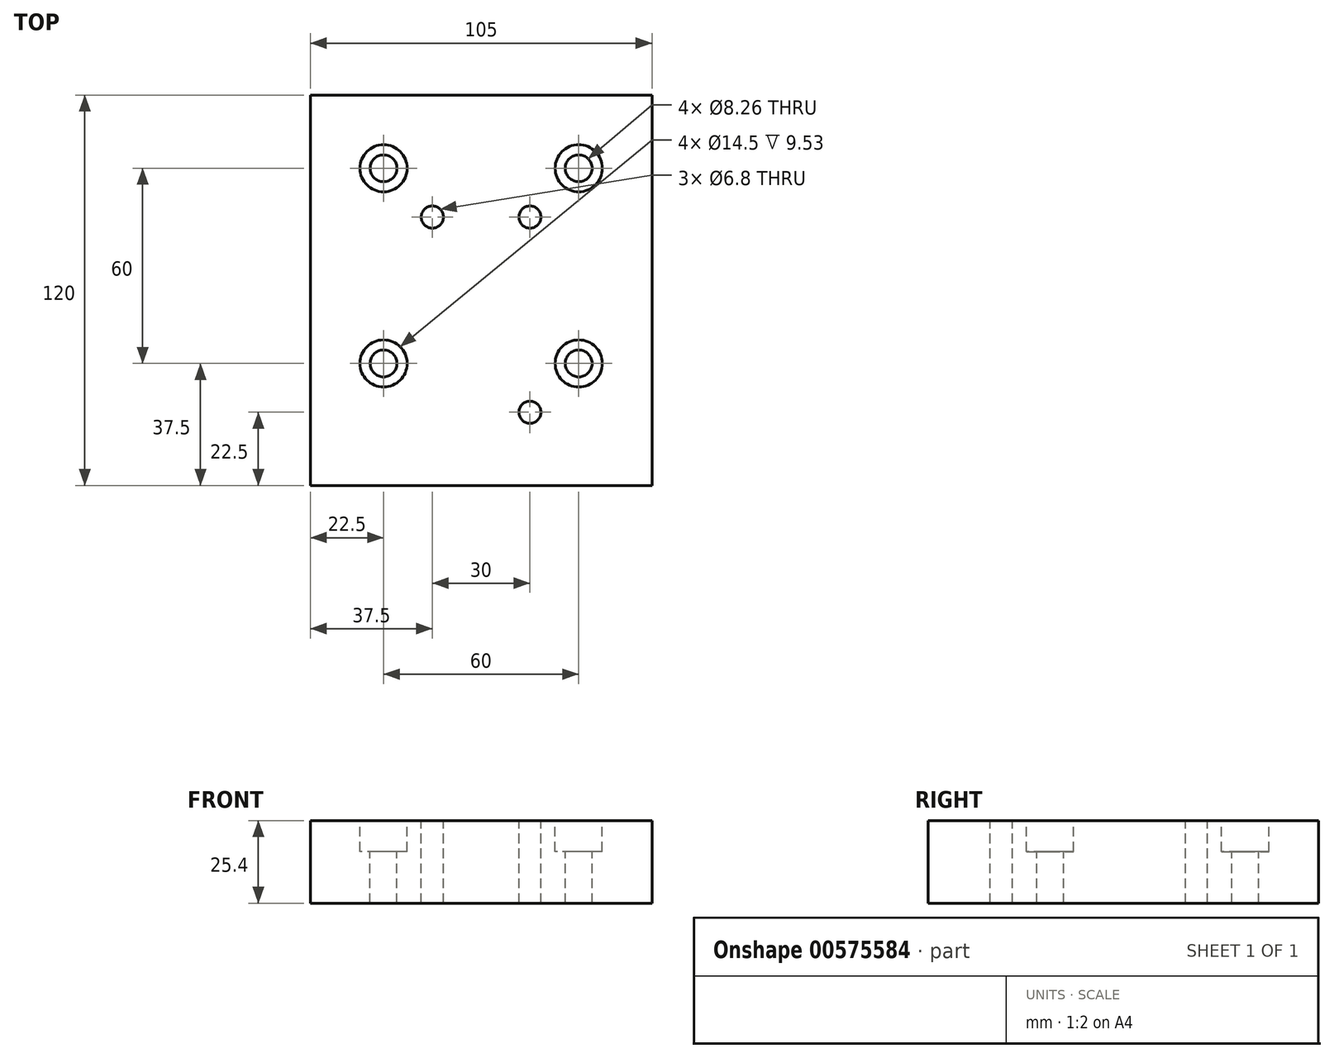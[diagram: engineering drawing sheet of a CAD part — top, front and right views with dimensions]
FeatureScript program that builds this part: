
annotation { "Feature Type Name" : "Feature", "Feature Type Description" : "" }
export const myFeature = defineFeature(function(context is Context, id is Id, definition is map)
    precondition{}
    {
        {
            var Q0;
            Q0=qCreatedBy(makeId("Top.planeOp"),FACE);
            var sketch = newSketch(context, id + "F0", { "sketchPlane" : qUnion([Q0])});
            skLineSegment(sketch, "E0.bottom", {"start": v(-52.5, -60) * mm, "end": v(52.5, -60) * mm});
            skLineSegment(sketch, "E0.top", {"start": v(-52.5, 60) * mm, "end": v(52.5, 60) * mm});
            skLineSegment(sketch, "E0.left", {"start": v(-52.5, -60) * mm, "end": v(-52.5, 60) * mm});
            skLineSegment(sketch, "E0.right", {"start": v(52.5, -60) * mm, "end": v(52.5, 60) * mm});
            skPoint(sketch, "E0.middle", {"position": v(0, 0) * mm});
            skSolve(sketch);
        }
        {
            var Q0;
            Q0=makeQuery(id+"F0.imprint","IMPRINT",FACE,{"disambiguationData":[TD([[makeQuery(id+"F0.imprint","IMPRINT",EDGE,{"derivedFrom":sQuery(id+"F0.wireOp",EDGE,"E0.bottom")}),1.0]])]});
            extrude(context, id + "F1", {"entities" : qUnion([Q0]), "depth" : 25.4 * mm, "offsetDistance" : 25 * mm});
        }
        {
            var Q0;
            Q0=makeQuery(id+"F1.opExtrude","CAP_FACE",FACE,{"disambiguationData":[OSD([sQuery(id+"F0.wireOp",EDGE,"E0.bottom"),sQuery(id+"F0.wireOp",EDGE,"E0.top"),sQuery(id+"F0.wireOp",EDGE,"E0.left"),sQuery(id+"F0.wireOp",EDGE,"E0.right")])],"isStart":false});
            var sketch = newSketch(context, id + "F2", { "sketchPlane" : qUnion([Q0])});
            skCircle(sketch, "E1", {"center": v(-30, 37.5) * mm, "radius": 2.02 * mm});
            skCircle(sketch, "E2", {"center": v(30, 37.5) * mm, "radius": 4.62 * mm});
            skCircle(sketch, "E3", {"center": v(30, -22.5) * mm, "radius": 3.17 * mm});
            skCircle(sketch, "E4", {"center": v(-30, -22.5) * mm, "radius": 3.76 * mm});
            skSolve(sketch);
        }
        {
            var Q0;
            Q0=sQuery(id+"F2.wireOp",VERTEX,"E1.center");
            var Q1;
            Q1=sQuery(id+"F2.wireOp",VERTEX,"E2.center");
            var Q2;
            Q2=sQuery(id+"F2.wireOp",VERTEX,"E3.center");
            var Q3;
            Q3=sQuery(id+"F2.wireOp",VERTEX,"E4.center");
            var Q4;
            Q4=makeQuery(id+"F1.opExtrude","SWEPT_BODY",BODY,{"disambiguationData":[OSD([sQuery(id+"F0.wireOp",EDGE,"E0.bottom"),sQuery(id+"F0.wireOp",EDGE,"E0.top"),sQuery(id+"F0.wireOp",EDGE,"E0.left"),sQuery(id+"F0.wireOp",EDGE,"E0.right")])]});
            hole(context, id + "F3", {"style" : HoleStyle.C_BORE, "endStyle" : HoleEndStyle.THROUGH, "holeDiameter" : 8.26 * mm, "cBoreDiameter" : 14.5 * mm, "cBoreDepth" : 9.53 * mm, "isTappedThrough" : true, "tappedDepth" : 12 * mm, "tapClearance" : 3, "locations" : qUnion([Q0, Q1, Q2, Q3]), "scope" : qUnion([Q4]), "majorDiameter" : 5 * mm});
        }
        {
            var Q0;
            Q0=makeQuery(id+"F1.opExtrude","CAP_FACE",FACE,{"disambiguationData":[OSD([sQuery(id+"F0.wireOp",EDGE,"E0.bottom"),sQuery(id+"F0.wireOp",EDGE,"E0.top"),sQuery(id+"F0.wireOp",EDGE,"E0.left"),sQuery(id+"F0.wireOp",EDGE,"E0.right")])],"isStart":false});
            var sketch = newSketch(context, id + "F4", { "sketchPlane" : qUnion([Q0])});
            skCircle(sketch, "E5", {"center": v(15, 22.5) * mm, "radius": 2.8 * mm});
            skCircle(sketch, "E6", {"center": v(-15, 22.5) * mm, "radius": 3.23 * mm});
            skCircle(sketch, "E7", {"center": v(15, -37.5) * mm, "radius": 2.8 * mm});
            skSolve(sketch);
        }
        {
            var Q0;
            Q0=sQuery(id+"F4.wireOp",VERTEX,"E7.center");
            var Q1;
            Q1=sQuery(id+"F4.wireOp",VERTEX,"E5.center");
            var Q2;
            Q2=sQuery(id+"F4.wireOp",VERTEX,"E6.center");
            var Q3;
            Q3=makeQuery(id+"F1.opExtrude","SWEPT_BODY",BODY,{"disambiguationData":[OSD([sQuery(id+"F0.wireOp",EDGE,"E0.bottom"),sQuery(id+"F0.wireOp",EDGE,"E0.top"),sQuery(id+"F0.wireOp",EDGE,"E0.left"),sQuery(id+"F0.wireOp",EDGE,"E0.right")])]});
            hole(context, id + "F5", {"style" : HoleStyle.SIMPLE, "endStyle" : HoleEndStyle.THROUGH, "standardTappedOrClearance" : lookupTablePath({ "standard" : "ISO", "engagement" : "75%", "pitch" : "1.25 mm", "size" : "M8", "type" : "Tapped" }), "standardBlindInLast" : lookupTablePath({ "standard" : "ISO", "engagement" : "75%", "pitch" : "1.25 mm", "size" : "M8", "type" : "Tapped" }), "holeDiameter" : 6.8 * mm, "showTappedDepth" : true, "isTappedThrough" : true, "tappedDepth" : 12 * mm, "tapClearance" : 3, "locations" : qUnion([Q0, Q1, Q2]), "scope" : qUnion([Q3]), "majorDiameter" : 8 * mm});
        }
    });
